# Revit family: TWT9053WM
name_source: partatom
category: Lighting Fixtures
revit_build: Autodesk Revit 2016 (Build: 20150714_1515(x64)
units: mm (PartAtom-declared; Revit-internal decimal feet)

## family parameters
Always vertical = Yes
Cut with Voids When Loaded = No
Light Source = No
OmniClass Number = 23.80.70.00
OmniClass Title = Lighting
Part Type = Normal
Room Calculation Point = No
Round Connector Dimension = Use Diameter
Shared = No
Work Plane-Based = No

## types (3) — shared parameters
Body Material = Plastic
Color = RAL9003
Customs Code = 94056080
Description = Self-Contained LED Exit Light with 3 h Battery and Self Testing
ETIM Product Class = EC001957
Electrical Installation = 2/3 x 2,5 mm² -o-
Feature = Lumi Test
GTIN Code = 6438045010700
Glow Wire Test of Plastic Materials = 850 °C
Height = 202 mm  [stored 0.66273 ft]
IP Class = IP44
Keynote = 23
Length = 268 mm  [stored 0.879265 ft]
Light Source = LED
Manufacturer = Teknoware Oy
Max Input Power VA = 5 VA
Max Input Power W = 0 W
Model = ESC 90
Mounting_Optional = Recess, Flag, Pendel
Mounting_Standard = Wall, Ceiling
Nominal Supply Voltage = 220-240 V, 50/60 Hz AC
Protection Class = II
Sähkönumero = 4211250
Sähkönumerot.fi -tuotesivu = http://www.sahkonumerot.fi
Temperature Range Min_Max = -5...+30 °C
Type Image = ESC90.jpg
URL = http://www.teknoware.com
Viewing Distance = 25000 mm  [stored 82.021 ft]
Weight = 0.60 kg
Width = 40 mm  [stored 0.131234 ft]

## per-type parameters (varying)
| type | Aperture for Recess Mounting | Pictogram Type | Product Code |
| Arrow left | 53 mm x 275 mm | OPASTE PB9004 | TWT9053WM |
| Arrow right | 53 mm x 275 mm | OPASTE PB9005 | TWT9053WM |
| Arrow down | 45 mm x 275 mm | OPASTE PB9006 | TWT9053WA |

note: [stored X ft] marks values corroborated as IEEE doubles in the binary element streams (Revit-internal decimal feet)

## geometry (parser evidence)
native form markers: Sweep x17
no freeform markers — native parametric forms only
